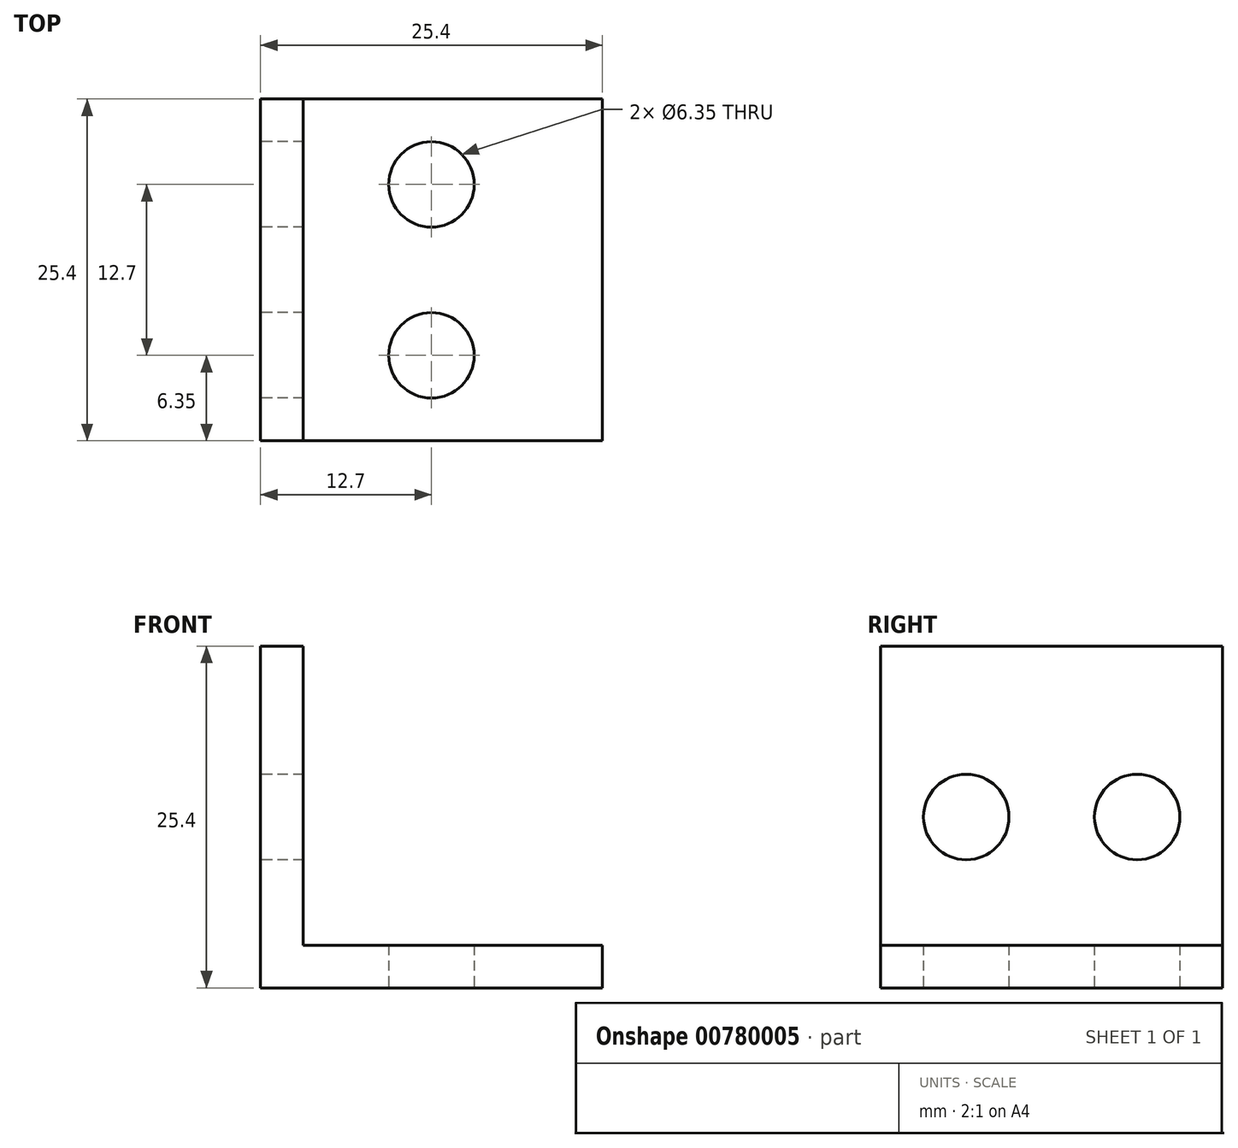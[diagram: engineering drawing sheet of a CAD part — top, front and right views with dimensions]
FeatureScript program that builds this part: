
annotation { "Feature Type Name" : "Feature", "Feature Type Description" : "" }
export const myFeature = defineFeature(function(context is Context, id is Id, definition is map)
    precondition{}
    {
        {
            var Q0;
            Q0=qCreatedBy(makeId("Front.planeOp"),FACE);
            var sketch = newSketch(context, id + "F0", { "sketchPlane" : qUnion([Q0])});
            skLineSegment(sketch, "E0", {"start": v(0, 0) * mm, "end": v(25.4, 0) * mm});
            skLineSegment(sketch, "E1", {"start": v(25.4, 0) * mm, "end": v(25.4, 3.18) * mm});
            skLineSegment(sketch, "E2", {"start": v(25.4, 3.18) * mm, "end": v(3.18, 3.17) * mm});
            skLineSegment(sketch, "E3", {"start": v(3.18, 3.17) * mm, "end": v(3.18, 25.4) * mm});
            skLineSegment(sketch, "E4", {"start": v(3.18, 25.4) * mm, "end": v(0, 25.4) * mm});
            skLineSegment(sketch, "E5", {"start": v(0, 25.4) * mm, "end": v(0, 0) * mm});
            skSolve(sketch);
        }
        {
            var Q0;
            Q0 = qSketchRegion(id + "F0", true);
            extrude(context, id + "F1", {"entities" : qUnion([Q0]), "depth" : 25.4 * mm, "offsetDistance" : 25.4 * mm});
        }
        {
            var Q0;
            Q0=makeQuery(id+"F1.opExtrude","SWEPT_FACE",FACE,{"disambiguationData":[OSD([sQuery(id+"F0.wireOp",EDGE,"E5")])]});
            var sketch = newSketch(context, id + "F2", { "sketchPlane" : qUnion([Q0])});
            skLineSegment(sketch, "E6", {"start": v(0, 12.7) * mm, "end": v(25.4, 12.7) * mm, "construction": true});
            skCircle(sketch, "E7", {"center": v(6.35, 12.7) * mm, "radius": 3.18 * mm});
            skCircle(sketch, "E8", {"center": v(19.05, 12.7) * mm, "radius": 3.18 * mm});
            skSolve(sketch);
        }
        {
            var Q0;
            Q0 = qSketchRegion(id + "F2", true);
            extrude(context, id + "F3", {"entities" : qUnion([Q0]), "operationType" : NewBodyOperationType.REMOVE, "oppositeDirection" : true, "depth" : 25.4 * mm, "offsetDistance" : 25.4 * mm});
        }
        {
            var Q0;
            Q0=makeQuery(id+"F1.opExtrude","SWEPT_FACE",FACE,{"disambiguationData":[OSD([sQuery(id+"F0.wireOp",EDGE,"E0")])]});
            var sketch = newSketch(context, id + "F4", { "sketchPlane" : qUnion([Q0])});
            skLineSegment(sketch, "E9", {"start": v(12.7, 25.4) * mm, "end": v(12.7, 0) * mm, "construction": true});
            skCircle(sketch, "E10", {"center": v(12.7, 19.05) * mm, "radius": 3.18 * mm});
            skCircle(sketch, "E11", {"center": v(12.7, 6.35) * mm, "radius": 3.18 * mm});
            skSolve(sketch);
        }
        {
            var Q0;
            Q0 = qSketchRegion(id + "F4", true);
            extrude(context, id + "F5", {"entities" : qUnion([Q0]), "operationType" : NewBodyOperationType.REMOVE, "oppositeDirection" : true, "depth" : 25.4 * mm, "offsetDistance" : 25.4 * mm});
        }
    });
